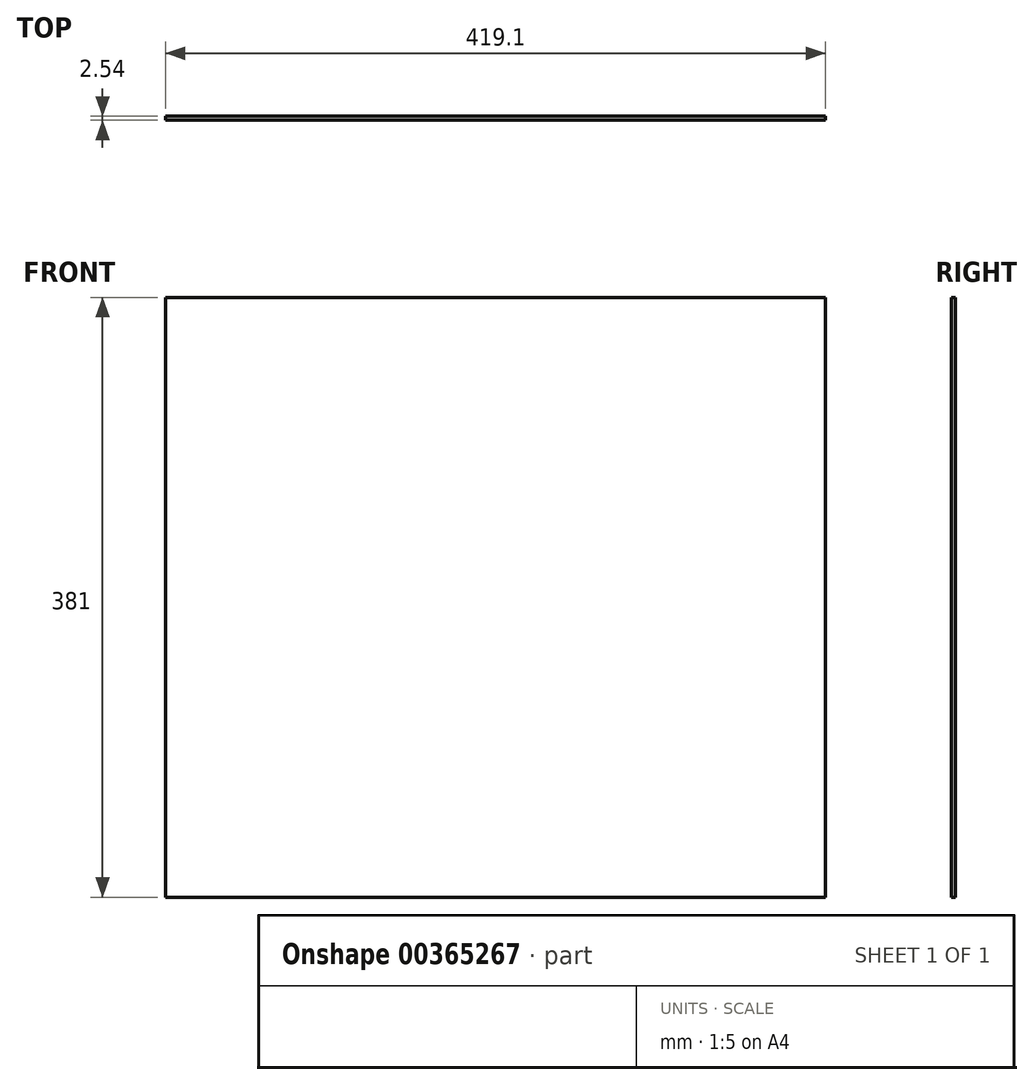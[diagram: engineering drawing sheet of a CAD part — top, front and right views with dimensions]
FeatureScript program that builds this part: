
annotation { "Feature Type Name" : "Feature", "Feature Type Description" : "" }
export const myFeature = defineFeature(function(context is Context, id is Id, definition is map)
    precondition{}
    {
        {
            var Q0;
            Q0=qCreatedBy(makeId("Front.planeOp"),FACE);
            var sketch = newSketch(context, id + "F0", { "sketchPlane" : qUnion([Q0])});
            skLineSegment(sketch, "E0.bottom", {"start": v(-207.78, 262.66) * mm, "end": v(211.32, 262.66) * mm});
            skLineSegment(sketch, "E0.top", {"start": v(-207.78, -118.34) * mm, "end": v(211.32, -118.34) * mm});
            skLineSegment(sketch, "E0.left", {"start": v(-207.78, 262.66) * mm, "end": v(-207.78, -118.34) * mm});
            skLineSegment(sketch, "E0.right", {"start": v(211.32, 262.66) * mm, "end": v(211.32, -118.34) * mm});
            skSolve(sketch);
        }
        {
            var Q0;
            Q0=qSketchRegion(id+"F0",true);
            extrude(context, id + "F1", {"entities" : qUnion([Q0]), "depth" : 2.54 * mm});
        }
    });
